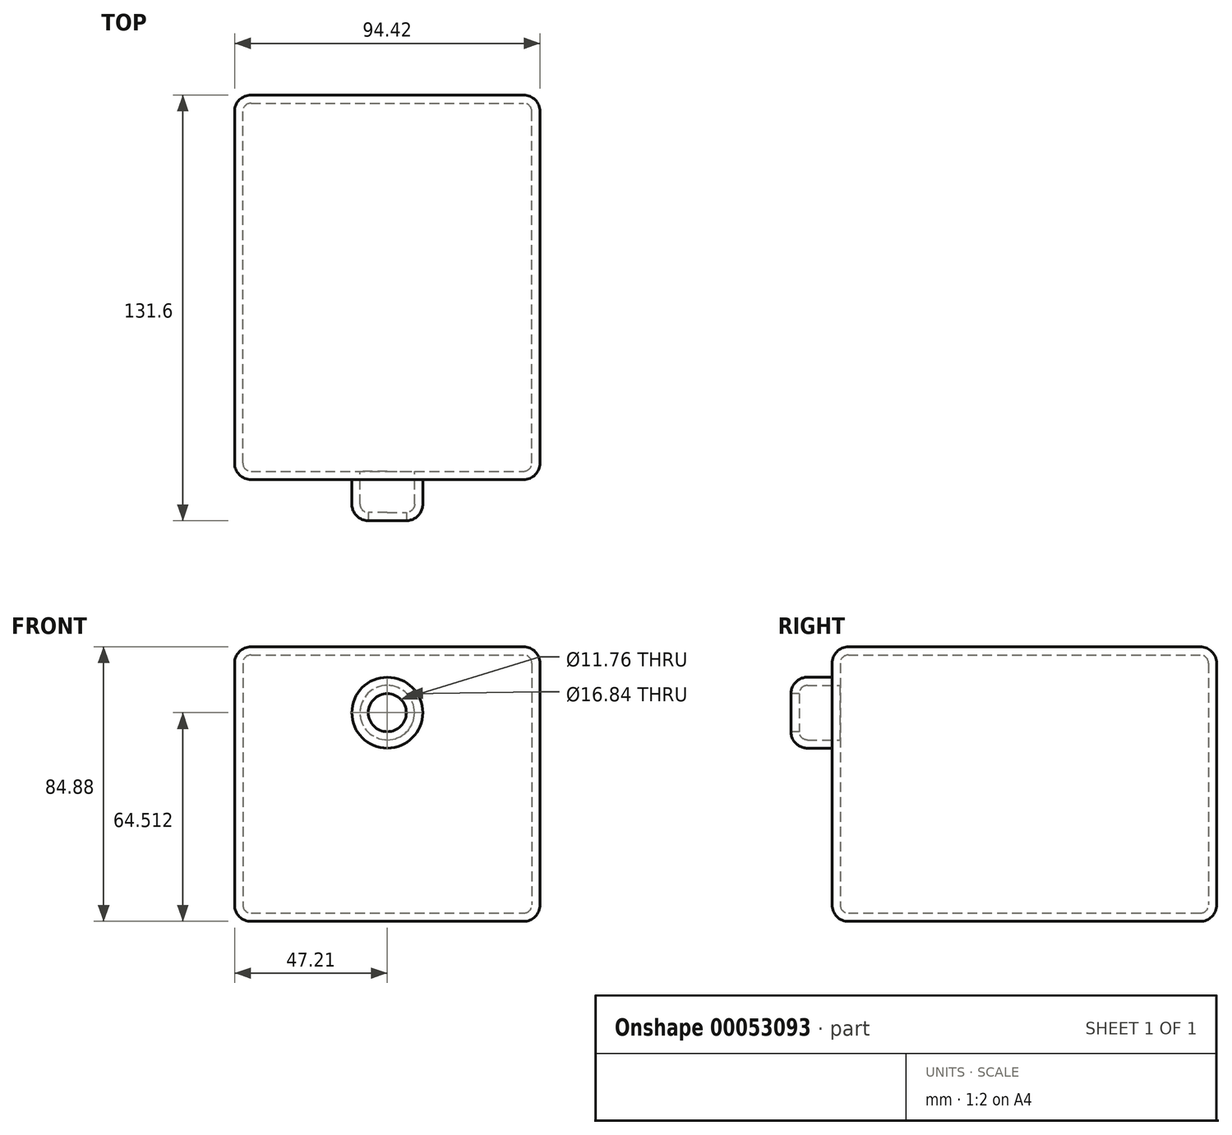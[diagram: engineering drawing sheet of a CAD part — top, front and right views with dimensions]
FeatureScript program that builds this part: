
annotation { "Feature Type Name" : "Feature", "Feature Type Description" : "" }
export const myFeature = defineFeature(function(context is Context, id is Id, definition is map)
    precondition{}
    {
        {
            var Q0;
            Q0=qCreatedBy(makeId("Top.planeOp"),FACE);
            var sketch = newSketch(context, id + "F0", { "sketchPlane" : qUnion([Q0])});
            skLineSegment(sketch, "E0.rect.bottom", {"start": v(47.2, 59.45) * mm, "end": v(-47.2, 59.45) * mm});
            skLineSegment(sketch, "E0.rect.top", {"start": v(47.2, -59.45) * mm, "end": v(-47.2, -59.45) * mm});
            skLineSegment(sketch, "E0.rect.left", {"start": v(47.2, 59.45) * mm, "end": v(47.2, -59.45) * mm});
            skLineSegment(sketch, "E0.rect.right", {"start": v(-47.2, 59.45) * mm, "end": v(-47.2, -59.45) * mm});
            skPoint(sketch, "E0.rect.middle", {"position": v(0, 0) * mm});
            skSolve(sketch);
        }
        {
            var Q0;
            Q0=makeQuery(id+"F0.imprint","IMPRINT",FACE,{"disambiguationData":[TD([[makeQuery(id+"F0.imprint","IMPRINT",EDGE,{"derivedFrom":sQuery(id+"F0.wireOp",EDGE,"E0.rect.bottom")}),1.0]])]});
            extrude(context, id + "F1", {"entities" : qUnion([Q0]), "depth" : 84.88 * mm});
        }
        {
            var Q0;
            Q0=makeQuery(id+"F1.opExtrude","SWEPT_FACE",FACE,{"disambiguationData":[OSD([sQuery(id+"F0.wireOp",EDGE,"E0.rect.top")])]});
            var sketch = newSketch(context, id + "F2", { "sketchPlane" : qUnion([Q0])});
            skCircle(sketch, "E1", {"center": v(0, 64.51) * mm, "radius": 10.96 * mm});
            skSolve(sketch);
        }
        {
            var Q0;
            Q0=makeQuery(id+"F2.imprint","IMPRINT",FACE,{"disambiguationData":[TD([[makeQuery(id+"F2.imprint","IMPRINT",EDGE,{"derivedFrom":sQuery(id+"F2.wireOp",EDGE,"E1")}),1.0]])]});
            extrude(context, id + "F3", {"entities" : qUnion([Q0]), "operationType" : NewBodyOperationType.ADD, "depth" : 12.7 * mm});
        }
        {
            var Q0;
            Q0=makeQuery(id+"F1.opExtrude","CAP_EDGE",EDGE,{"disambiguationData":[OSD([sQuery(id+"F0.wireOp",EDGE,"E0.rect.top")])],"isStart":false});
            var Q1;
            Q1=makeQuery(id+"F1.opExtrude","CAP_EDGE",EDGE,{"disambiguationData":[OSD([sQuery(id+"F0.wireOp",EDGE,"E0.rect.left")])],"isStart":false});
            var Q2;
            Q2=makeQuery(id+"F1.opExtrude","CAP_EDGE",EDGE,{"disambiguationData":[OSD([sQuery(id+"F0.wireOp",EDGE,"E0.rect.left")])],"isStart":true});
            var Q3;
            Q3=makeQuery(id+"F1.opExtrude","CAP_EDGE",EDGE,{"disambiguationData":[OSD([sQuery(id+"F0.wireOp",EDGE,"E0.rect.top")])],"isStart":true});
            var Q4;
            Q4=makeQuery(id+"F1.opExtrude","CAP_EDGE",EDGE,{"disambiguationData":[OSD([sQuery(id+"F0.wireOp",EDGE,"E0.rect.bottom")])],"isStart":false});
            var Q5;
            Q5=makeQuery(id+"F1.opExtrude","CAP_EDGE",EDGE,{"disambiguationData":[OSD([sQuery(id+"F0.wireOp",EDGE,"E0.rect.right")])],"isStart":false});
            var Q6;
            Q6=makeQuery(id+"F1.opExtrude","CAP_EDGE",EDGE,{"disambiguationData":[OSD([sQuery(id+"F0.wireOp",EDGE,"E0.rect.bottom")])],"isStart":true});
            var Q7;
            Q7=makeQuery(id+"F1.opExtrude","SWEPT_EDGE",EDGE,{"disambiguationData":[OSD([sQuery(id+"F0.wireOp",EDGE,"E0.rect.bottom"),sQuery(id+"F0.wireOp",EDGE,"E0.rect.left")])]});
            var Q8;
            Q8=makeQuery(id+"F1.opExtrude","SWEPT_EDGE",EDGE,{"disambiguationData":[OSD([sQuery(id+"F0.wireOp",EDGE,"E0.rect.top"),sQuery(id+"F0.wireOp",EDGE,"E0.rect.left")])]});
            var Q9;
            Q9=makeQuery(id+"F1.opExtrude","SWEPT_EDGE",EDGE,{"disambiguationData":[OSD([sQuery(id+"F0.wireOp",EDGE,"E0.rect.bottom"),sQuery(id+"F0.wireOp",EDGE,"E0.rect.right")])]});
            var Q10;
            Q10=makeQuery(id+"F1.opExtrude","CAP_EDGE",EDGE,{"disambiguationData":[OSD([sQuery(id+"F0.wireOp",EDGE,"E0.rect.right")])],"isStart":true});
            var Q11;
            Q11=makeQuery(id+"F1.opExtrude","SWEPT_EDGE",EDGE,{"disambiguationData":[OSD([sQuery(id+"F0.wireOp",EDGE,"E0.rect.top"),sQuery(id+"F0.wireOp",EDGE,"E0.rect.right")])]});
            var Q12;
            Q12=makeQuery(id+"F3.opExtrude","CAP_FACE",FACE,{"disambiguationData":[OSD([sQuery(id+"F2.wireOp",EDGE,"E1")])],"isStart":false});
            fillet(context, id + "F4", {"entities" : qUnion([Q0, Q1, Q2, Q3, Q4, Q5, Q6, Q7, Q8, Q9, Q10, Q11, Q12]), "radius" : 5.08 * mm, "tangentPropagation" : true, "allowEdgeOverflow" : false});
        }
        {
            var Q0;
            Q0=makeQuery(id+"F3.opExtrude","CAP_FACE",FACE,{"disambiguationData":[OSD([sQuery(id+"F2.wireOp",EDGE,"E1")])],"isStart":false});
            shell(context, id + "F5", {"entities" : qUnion([Q0]), "thickness" : 2.54 * mm});
        }
    });
